FCSTD DOCUMENT  (FreeCAD 0.18R16131 (Git))
Label: YDriveLager_Ver2
License: All rights reserved
LicenseURL: http://en.wikipedia.org/wiki/All_rights_reserved
objects: Part::Cut×51, Part::Cylinder×34, Part::Box×11, Part::Feature×8, Part::Fillet×4, Part::Chamfer×1, Part::MultiFuse×1
note: 110 computed .brp shape members not serialized (recipe doc carries the construction recipe); baked Part::Feature solids carry a one-line shape summary decoded from their .brp

FEATURE [Part::Box] Box  label="Würfel"
  AttacherType = Attacher::AttachEngine3D
  Height = 5
  Length = 84
  Width = 139.6
FEATURE [Part::Cylinder] Cylinder  label="Zylinder"
  Angle = 360
  AttacherType = Attacher::AttachEngine3D
  Height = 40
  Placement = pos=(6,6,0) rot=(0,0,1;0rad)
  Radius = 3
FEATURE [Part::Cylinder] Cylinder001  label="Zylinder001"
  Angle = 360
  AttacherType = Attacher::AttachEngine3D
  Height = 40
  Placement = pos=(6,34,0) rot=(0,0,1;0rad)
  Radius = 3
FEATURE [Part::Cylinder] Cylinder003  label="Zylinder003"
  Angle = 360
  AttacherType = Attacher::AttachEngine3D
  Height = 40
  Placement = pos=(6,133.6,0) rot=(0,0,1;0rad)
  Radius = 3
FEATURE [Part::Cylinder] Cylinder004  label="Zylinder004"
  Angle = 360
  AttacherType = Attacher::AttachEngine3D
  Height = 40
  Placement = pos=(32,6,0) rot=(0,0,1;0rad)
  Radius = 3
FEATURE [Part::Cylinder] Cylinder006  label="Zylinder006"
  Angle = 360
  AttacherType = Attacher::AttachEngine3D
  Height = 40
  Placement = pos=(6,106.6,0) rot=(0,0,1;0rad)
  Radius = 3
FEATURE [Part::Cylinder] Cylinder007  label="Zylinder007"
  Angle = 360
  AttacherType = Attacher::AttachEngine3D
  Height = 40
  Placement = pos=(31,133.6,0) rot=(0,0,1;0rad)
  Radius = 3
FEATURE [Part::Cylinder] Cylinder008  label="Zylinder008"
  Angle = 360
  AttacherType = Attacher::AttachEngine3D
  Height = 40
  Placement = pos=(19,20,0) rot=(0,0,1;0rad)
  Radius = 4
FEATURE [Part::Cylinder] Cylinder009  label="Zylinder009"
  Angle = 360
  AttacherType = Attacher::AttachEngine3D
  Height = 40
  Placement = pos=(19,120.1,0) rot=(0,0,1;0rad)
  Radius = 4
FEATURE [Part::Cylinder] Cylinder010  label="Zylinder010"
  Angle = 360
  AttacherType = Attacher::AttachEngine3D
  Height = 40
  Placement = pos=(52,6,0) rot=(0,0,1;0rad)
  Radius = 3
FEATURE [Part::Cylinder] Cylinder011  label="Zylinder011"
  Angle = 360
  AttacherType = Attacher::AttachEngine3D
  Height = 40
  Placement = pos=(78,6,0) rot=(0,0,1;0rad)
  Radius = 3
FEATURE [Part::Cylinder] Cylinder013  label="Zylinder013"
  Angle = 360
  AttacherType = Attacher::AttachEngine3D
  Height = 40
  Placement = pos=(52,34,0) rot=(0,0,1;0rad)
  Radius = 3
FEATURE [Part::Cylinder] Cylinder015  label="Zylinder015"
  Angle = 360
  AttacherType = Attacher::AttachEngine3D
  Height = 40
  Placement = pos=(52,106.6,0) rot=(0,0,1;0rad)
  Radius = 3
FEATURE [Part::Cylinder] Cylinder016  label="Zylinder016"
  Angle = 360
  AttacherType = Attacher::AttachEngine3D
  Height = 40
  Placement = pos=(52,133.6,0) rot=(0,0,1;0rad)
  Radius = 3
FEATURE [Part::Cylinder] Cylinder017  label="Zylinder017"
  Angle = 360
  AttacherType = Attacher::AttachEngine3D
  Height = 40
  Placement = pos=(78,133.6,0) rot=(0,0,1;0rad)
  Radius = 3
FEATURE [Part::Cylinder] Cylinder018  label="Zylinder018"
  Angle = 360
  AttacherType = Attacher::AttachEngine3D
  Height = 40
  Placement = pos=(65,20,0) rot=(0,0,1;0rad)
  Radius = 4
FEATURE [Part::Cylinder] Cylinder019  label="Zylinder019"
  Angle = 360
  AttacherType = Attacher::AttachEngine3D
  Height = 40
  Placement = pos=(65,120.1,0) rot=(0,0,1;0rad)
  Radius = 4
FEATURE [Part::Box] Box003  label="Würfel003"
  AttacherType = Attacher::AttachEngine3D
  Height = 30
  Length = 63
  Placement = pos=(0,47.8,0) rot=(0,0,1;0rad)
  Width = 44
FEATURE [Part::Cylinder] Cylinder020  label="Zylinder020"
  Angle = 360
  AttacherType = Attacher::AttachEngine3D
  Height = 40
  Placement = pos=(40,69.8,0) rot=(0,0,1;0rad)
  Radius = 12
FEATURE [Part::Cylinder] Cylinder021  label="Zylinder021"
  Angle = 360
  AttacherType = Attacher::AttachEngine3D
  Height = 40
  Placement = pos=(28,29,5) rot=(0,0,1;0rad)
  Radius = 4.1
FEATURE [Part::Cylinder] Cylinder022  label="Zylinder022"
  Angle = 360
  AttacherType = Attacher::AttachEngine3D
  Height = 40
  Placement = pos=(28,110.6,5) rot=(0,0,1;0rad)
  Radius = 4.1
FEATURE [Part::Box] Box005  label="Würfel005"
  AttacherType = Attacher::AttachEngine3D
  Height = 40
  Length = 15.6
  Placement = pos=(63.95,28.95,5) rot=(0,0,1;0rad)
  Width = 15.6
FEATURE [Part::Box] Box007  label="Würfel007"
  AttacherType = Attacher::AttachEngine3D
  Height = 40
  Length = 15.6
  Placement = pos=(63.95,95.05,5) rot=(0,0,1;0rad)
  Width = 15.6
FEATURE [Part::Box] Box008  label="Würfel008"
  AttacherType = Attacher::AttachEngine3D
  Height = 35
  Length = 64
  Placement = pos=(20,0,0) rot=(0,0,1;0rad)
  Width = 139.6
FEATURE [Part::Cylinder] Cylinder024  label="Zylinder024"
  Angle = 360
  AttacherType = Attacher::AttachEngine3D
  Height = 40
  Placement = pos=(24.5,54.3,0) rot=(0,0,1;0rad)
  Radius = 2
FEATURE [Part::Cylinder] Cylinder025  label="Zylinder025"
  Angle = 360
  AttacherType = Attacher::AttachEngine3D
  Height = 40
  Placement = pos=(55.5,54.3,0) rot=(0,0,1;0rad)
  Radius = 2
FEATURE [Part::Cylinder] Cylinder026  label="Zylinder026"
  Angle = 360
  AttacherType = Attacher::AttachEngine3D
  Height = 40
  Placement = pos=(55.5,85.3,0) rot=(0,0,1;0rad)
  Radius = 2
FEATURE [Part::Cylinder] Cylinder027  label="Zylinder027"
  Angle = 360
  AttacherType = Attacher::AttachEngine3D
  Height = 40
  Placement = pos=(24.5,85.3,0) rot=(0,0,1;0rad)
  Radius = 2
FEATURE [Part::Cylinder] Cylinder028  label="Zylinder028"
  Angle = 360
  AttacherType = Attacher::AttachEngine3D
  Height = 40
  Placement = pos=(78,133.6,6) rot=(0,0,1;0rad)
  Radius = 5
FEATURE [Part::Cylinder] Cylinder029  label="Zylinder029"
  Angle = 360
  AttacherType = Attacher::AttachEngine3D
  Height = 40
  Placement = pos=(78,6,6) rot=(0,0,1;0rad)
  Radius = 5
FEATURE [Part::Cylinder] Cylinder030  label="Zylinder030"
  Angle = 360
  AttacherType = Attacher::AttachEngine3D
  Height = 40
  Placement = pos=(31,133.6,6) rot=(0,0,1;0rad)
  Radius = 5
FEATURE [Part::Cylinder] Cylinder031  label="Zylinder031"
  Angle = 360
  AttacherType = Attacher::AttachEngine3D
  Height = 40
  Placement = pos=(32,6,6) rot=(0,0,1;0rad)
  Radius = 5
FEATURE [Part::Box] Box009  label="Würfel009"
  AttacherType = Attacher::AttachEngine3D
  Height = 40
  Length = 5
  Placement = pos=(79,49.2,0) rot=(0,0,1;0rad)
  Width = 40
FEATURE [Part::Feature] Part__Feature008  label="ScrewTap-M4x30_"
  Placement = pos=(59,57.8,10) rot=(0,-1,0;1.5708rad)
  shape: bbox 31.5 x 6.156 x 5.739 mm, 178 faces (baked)
FEATURE [Part::Feature] Part__Feature009  label="ScrewTap-M4x30_001"
  Placement = pos=(59,57.8,25) rot=(0,-1,0;1.5708rad)
  shape: bbox 31.5 x 6.156 x 5.739 mm, 178 faces (baked)
FEATURE [Part::Feature] Part__Feature010  label="ScrewTap-M4x30_002"
  Placement = pos=(59,81.8,10) rot=(0,-1,0;1.5708rad)
  shape: bbox 31.5 x 6.156 x 5.739 mm, 178 faces (baked)
FEATURE [Part::Feature] Part__Feature011  label="ScrewTap-M4x30_003"
  Placement = pos=(59,81.8,25) rot=(0,-1,0;1.5708rad)
  shape: bbox 31.5 x 6.156 x 5.739 mm, 178 faces (baked)
FEATURE [Part::Feature] Part__Feature012  label="ScrewTap-M4x30_004"
  Placement = pos=(38,43.8,10) rot=(0,1,0;1.5708rad)
  shape: bbox 31.5 x 6.156 x 5.739 mm, 178 faces (baked)
FEATURE [Part::Feature] Part__Feature013  label="ScrewTap-M4x30_005"
  Placement = pos=(38,95.8,25) rot=(0,1,0;1.5708rad)
  shape: bbox 31.5 x 6.156 x 5.739 mm, 178 faces (baked)
FEATURE [Part::Feature] Part__Feature014  label="ScrewTap-M4x30_006"
  Placement = pos=(38,43.8,25) rot=(0,1,0;1.5708rad)
  shape: bbox 31.5 x 6.156 x 5.739 mm, 178 faces (baked)
FEATURE [Part::Feature] Part__Feature015  label="ScrewTap-M4x30_007"
  Placement = pos=(38,95.8,10) rot=(0,1,0;1.5708rad)
  shape: bbox 31.5 x 6.156 x 5.739 mm, 178 faces (baked)
FEATURE [Part::Box] Box011  label="Würfel011"
  AttacherType = Attacher::AttachEngine3D
  Height = 40
  Length = 37
  Placement = pos=(0,63.8,0) rot=(0,0,1;0rad)
  Width = 12
FEATURE [Part::Chamfer] Chamfer
  Base = -> Box008
  Edges = 2 edges: [Edge10 r1=30 r2=22,Edge12 r1=30 r2=22]
FEATURE [Part::MultiFuse] Fusion
  Shapes = -> [Box,Chamfer]
FEATURE [Part::Cut] Cut
  Base = -> Fusion
  Tool = -> Box003
FEATURE [Part::Cut] Cut001
  Base = -> Cut
  Tool = -> Cylinder020
FEATURE [Part::Cut] Cut002
  Base = -> Cut001
  Tool = -> Box011
FEATURE [Part::Cut] Cut003
  Base = -> Cut002
  Tool = -> Cylinder027
FEATURE [Part::Cut] Cut004
  Base = -> Cut003
  Tool = -> Cylinder026
FEATURE [Part::Cut] Cut005
  Base = -> Cut004
  Tool = -> Cylinder025
FEATURE [Part::Cut] Cut006
  Base = -> Cut005
  Tool = -> Cylinder024
FEATURE [Part::Cylinder] Cylinder032  label="Zylinder032"
  Angle = 360
  AttacherType = Attacher::AttachEngine3D
  Height = 40
  Placement = pos=(52,34,10) rot=(0,0,1;0rad)
  Radius = 5
FEATURE [Part::Cylinder] Cylinder033  label="Zylinder033"
  Angle = 360
  AttacherType = Attacher::AttachEngine3D
  Height = 40
  Placement = pos=(52,106.6,10) rot=(0,0,1;0rad)
  Radius = 5
FEATURE [Part::Cylinder] Cylinder034  label="Zylinder034"
  Angle = 360
  AttacherType = Attacher::AttachEngine3D
  Height = 40
  Placement = pos=(52,6,6) rot=(0,0,1;0rad)
  Radius = 5
FEATURE [Part::Cylinder] Cylinder035  label="Zylinder035"
  Angle = 360
  AttacherType = Attacher::AttachEngine3D
  Height = 40
  Placement = pos=(52,133.6,6) rot=(0,0,1;0rad)
  Radius = 5
FEATURE [Part::Box] Box012  label="Würfel012"
  AttacherType = Attacher::AttachEngine3D
  Height = 40
  Length = 40
  Placement = pos=(29,28,10) rot=(0,0,1;0.20944rad)
  Width = 2
FEATURE [Part::Box] Box013  label="Würfel013"
  AttacherType = Attacher::AttachEngine3D
  Height = 40
  Length = 40
  Placement = pos=(29,110,10) rot=(0,0,1;-0.20944rad)
  Width = 2
FEATURE [Part::Cut] Cut007
  Base = -> Cut006
  Tool = -> Cylinder022
FEATURE [Part::Cut] Cut008
  Base = -> Cut007
  Tool = -> Box013
FEATURE [Part::Cut] Cut009
  Base = -> Cut008
  Tool = -> Box012
FEATURE [Part::Cut] Cut010
  Base = -> Cut009
  Tool = -> Cylinder021
FEATURE [Part::Cut] Cut011
  Base = -> Cut010
  Tool = -> Box007
FEATURE [Part::Cut] Cut012
  Base = -> Cut011
  Tool = -> Box005
FEATURE [Part::Cut] Cut013
  Base = -> Cut012
  Tool = -> Cylinder033
FEATURE [Part::Cut] Cut014
  Base = -> Cut013
  Tool = -> Cylinder015
FEATURE [Part::Cut] Cut015
  Base = -> Cut014
  Tool = -> Cylinder032
FEATURE [Part::Cut] Cut016
  Base = -> Cut015
  Tool = -> Cylinder013
FEATURE [Part::Cut] Cut017
  Base = -> Cut016
  Tool = -> Cylinder008
FEATURE [Part::Cut] Cut018
  Base = -> Cut017
  Tool = -> Cylinder018
FEATURE [Part::Cut] Cut019
  Base = -> Cut018
  Tool = -> Cylinder009
FEATURE [Part::Cut] Cut020
  Base = -> Cut019
  Tool = -> Cylinder019
FEATURE [Part::Cut] Cut021
  Base = -> Cut020
  Tool = -> Cylinder031
FEATURE [Part::Cut] Cut022
  Base = -> Cut021
  Tool = -> Cylinder004
FEATURE [Part::Cut] Cut023
  Base = -> Cut022
  Tool = -> Cylinder034
FEATURE [Part::Cut] Cut024
  Base = -> Cut023
  Tool = -> Cylinder029
FEATURE [Part::Cut] Cut025
  Base = -> Cut024
  Tool = -> Cylinder010
FEATURE [Part::Cut] Cut026
  Base = -> Cut025
  Tool = -> Cylinder011
FEATURE [Part::Cut] Cut027
  Base = -> Cut026
  Tool = -> Cylinder028
FEATURE [Part::Cut] Cut028
  Base = -> Cut027
  Tool = -> Cylinder035
FEATURE [Part::Cut] Cut029
  Base = -> Cut028
  Tool = -> Cylinder030
FEATURE [Part::Cut] Cut030
  Base = -> Cut029
  Tool = -> Cylinder017
FEATURE [Part::Cut] Cut031
  Base = -> Cut030
  Tool = -> Cylinder016
FEATURE [Part::Cut] Cut032
  Base = -> Cut031
  Tool = -> Cylinder007
FEATURE [Part::Cut] Cut033
  Base = -> Cut032
  Tool = -> Box009
FEATURE [Part::Cut] Cut034
  Base = -> Cut033
  Tool = -> Part__Feature009
FEATURE [Part::Cut] Cut035
  Base = -> Cut034
  Tool = -> Part__Feature010
FEATURE [Part::Cut] Cut036
  Base = -> Cut035
  Tool = -> Part__Feature008
FEATURE [Part::Cut] Cut037
  Base = -> Cut036
  Tool = -> Part__Feature011
FEATURE [Part::Cut] Cut038
  Base = -> Cut037
  Tool = -> Part__Feature013
FEATURE [Part::Cut] Cut039
  Base = -> Cut038
  Tool = -> Part__Feature014
FEATURE [Part::Cut] Cut040
  Base = -> Cut039
  Tool = -> Part__Feature015
FEATURE [Part::Cut] Cut041
  Base = -> Cut040
  Tool = -> Part__Feature012
FEATURE [Part::Cut] Cut042
  Base = -> Cut041
  Tool = -> Cylinder001
FEATURE [Part::Cut] Cut043
  Base = -> Cut042
  Tool = -> Cylinder
FEATURE [Part::Cylinder] Cylinder036  label="Zylinder036"
  Angle = 360
  AttacherType = Attacher::AttachEngine3D
  Height = 19
  Placement = pos=(45,-1.3,24) rot=(1,0,0;-1.5708rad)
  Radius = 5
FEATURE [Part::Cylinder] Cylinder037  label="Zylinder037"
  Angle = 360
  AttacherType = Attacher::AttachEngine3D
  Height = 140
  Placement = pos=(45,0,24) rot=(-1,0,0;1.5708rad)
  Radius = 2.6
FEATURE [Part::Box] Box014  label="Würfel014"
  AttacherType = Attacher::AttachEngine3D
  Height = 18
  Length = 8.5
  Placement = pos=(40.75,40,19.75) rot=(0,0,1;0rad)
  Width = 5
FEATURE [Part::Box] Box015  label="Würfel015"
  AttacherType = Attacher::AttachEngine3D
  Height = 18
  Length = 8.5
  Placement = pos=(40.75,94.6,19.75) rot=(0,0,1;0rad)
  Width = 5
FEATURE [Part::Cut] Cut044
  Base = -> Cut043
  Tool = -> Cylinder003
FEATURE [Part::Cut] Cut045
  Base = -> Cut044
  Tool = -> Cylinder006
FEATURE [Part::Cylinder] Cylinder038  label="Zylinder038"
  Angle = 360
  AttacherType = Attacher::AttachEngine3D
  Height = 19
  Placement = pos=(45,121.9,24) rot=(-1,0,0;1.5708rad)
  Radius = 5
FEATURE [Part::Cut] Cut046
  Base = -> Cut045
  Tool = -> Cylinder036
FEATURE [Part::Cut] Cut047
  Base = -> Cut046
  Tool = -> Cylinder038
FEATURE [Part::Cut] Cut048
  Base = -> Cut047
  Tool = -> Box015
FEATURE [Part::Cut] Cut049
  Base = -> Cut048
  Tool = -> Box014
FEATURE [Part::Cut] Cut050
  Base = -> Cut049
  Tool = -> Cylinder037
FEATURE [Part::Fillet] Fillet
  Base = -> Cut050
  Edges = 6 edges r=5: [Edge2,Edge4,Edge106,Edge190,Edge222,Edge445]
FEATURE [Part::Fillet] Fillet001
  Base = -> Fillet
  Edges = 22 edges r=0.5: [Edge4,Edge14,Edge16,Edge18,Edge22,Edge25,Edge55,Edge56,Edge58,Edge60,Edge62,Edge64,Edge65,Edge66,Edge67,Edge68,Edge69,Edge205,Edge206,Edge207,Edge209,Edge210]
FEATURE [Part::Fillet] Fillet002
  Base = -> Fillet001
  Edges = 20 edges r=0.5: [Edge27,Edge31,Edge32,Edge59,Edge60,Edge70,Edge72,Edge84,Edge85,Edge86,Edge87,Edge88,Edge89,Edge90,Edge91,Edge92,Edge93,Edge219,Edge224,Edge225]
FEATURE [Part::Fillet] Fillet003
  Base = -> Fillet002
  Edges = 16 edges r=0.5: [Edge287,Edge288,Edge289,Edge290,Edge312,Edge313,Edge314,Edge315,Edge334,Edge335,Edge336,Edge337,Edge338,Edge339,Edge340,Edge341]
